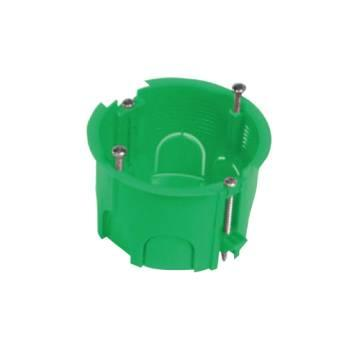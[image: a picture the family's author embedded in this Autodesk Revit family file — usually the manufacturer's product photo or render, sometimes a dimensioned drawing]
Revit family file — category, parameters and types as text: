
# Revit family: Building-FlushMountingEnclosures-GEWISS-24SC-GREENWALL-BOXES_ROUND
name_source: partatom
category: Apparecchi elettrici
revit_build: Autodesk Revit 2016 (Build: 20161004_0715(x64)
units: mm (PartAtom-declared; Revit-internal decimal feet)

## family parameters
Condiviso = Sì
Host = Superficie
Mantenere orientamento annotazione = Sì
Numero OmniClass = 23.80.30.14.24
Punto di calcolo locali = Sì
Quota connettore circolare = Usa diametro
Taglio con vuoti quando caricato = Sì
Tipo di parte = Normale
Titolo OmniClass = Junction Boxes

## types (1)
- GW24234PM - Halogen free - D.65x45
    Carico apparente = 0 VA
    Catalogue = BUILDING
    Catalogue Range = 24SC
    Characteristics = Halogen free
    Classificazione = Altro
    Description: = Round
    Descrizione = PLASTERBOARD W. ROUND BOX - GW
    Dimensions (mm) = Ã˜ 65x45
    EAN code = 8011564802025
    Electrocod = 0210
    Fixing supports axles distance = 60MM
    For walls = Plasterboard
    Glow Wire Test = 850°C
    IDF = 83853085-20e1-4058-a0e9-66de417eec9c
    IDT = d2635837-3151-40c3-856d-c8cfc8bd2e75
    IP degree = IP40
    Immagine tipo = GW24234PM.jpg
    Installation = Flush mounting enclosures
    Metallo = GEWISS - Elementi acciaio
    Modello = GW24234PM
    Operating temperature = -15 ÷ +60°C
    Produttore = GEWISS S.p.A.
    Profondità = 45 mm  [stored 0.147638 ft]
    Prospetto di default = 1219.2 mm  [stored 4 ft]
    SEO = Box
    Scatola = GEWISS - scatola a incasso
    Shock resistance = IK07
    Technical sheet = https://www.gewiss.com
    Thermo-pressure with ball = 70
    Type of material = Halogen-free in compliance with EN 60754-2
    URL = https://www.gewiss.com
    Version file RFA = 19.0
    Voltaggio = 0 V

note: source unit labels omitted for Thermo-pressure with ball — the stored unit's dimension contradicts the parameter name (converter mislabeling)

note: [stored X ft] marks values corroborated as IEEE doubles in the binary element streams (Revit-internal decimal feet)

## geometry (parser evidence)
native form markers: Blend x2, Sweep x2
no freeform markers — native parametric forms only
